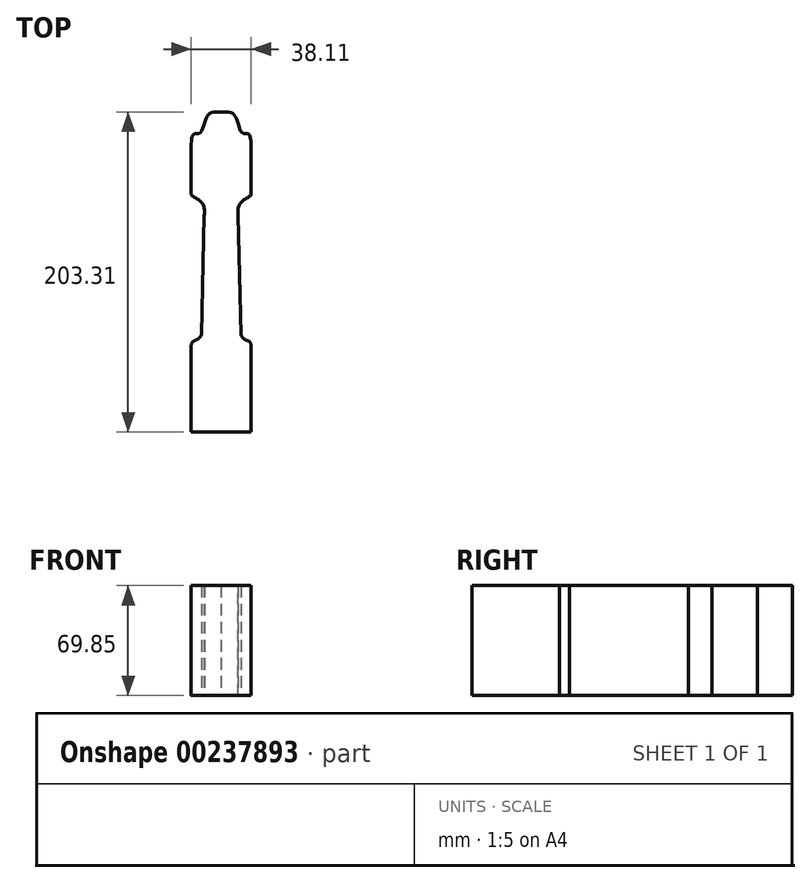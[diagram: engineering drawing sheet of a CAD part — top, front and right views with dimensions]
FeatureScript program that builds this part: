
annotation { "Feature Type Name" : "Feature", "Feature Type Description" : "" }
export const myFeature = defineFeature(function(context is Context, id is Id, definition is map)
    precondition{}
    {
        {
            var Q0;
            Q0=qCreatedBy(makeId("Top.planeOp"),FACE);
            var sketch = newSketch(context, id + "F0", { "sketchPlane" : qUnion([Q0])});
            skLineSegment(sketch, "E0", {"start": v(-63.39, 48.27) * mm, "end": v(-63.39, -154.93) * mm});
            skLineSegment(sketch, "E1", {"start": v(-170.06, 93.3) * mm, "end": v(-170.06, -109.9) * mm});
            skFitSpline(sketch, "E2.MirrorCS", {"points": [v(-170.06, 93.3) * mm, v(-178.63, 91.27) * mm, v(-183.26, 80.39) * mm, v(-187.5, 79.18) * mm, v(-189.1, 71.32) * mm], "startDerivative": vector(-38.08, 2.27) * mm, "endDerivative": vector(-0.76, -41.24) * mm});
            skFitSpline(sketch, "E3", {"points": [v(-189.05, 42.29) * mm, v(-188.9, 40.7) * mm, v(-184.87, 37.86) * mm, v(-181.25, 33.82) * mm, v(-180.84, 27.58) * mm], "startDerivative": vector(-1.25, -12.1) * mm, "endDerivative": vector(-1.29, -22.61) * mm});
            skLineSegment(sketch, "E4", {"start": v(-189.1, -109.9) * mm, "end": v(-189.1, -54.56) * mm});
            skLineSegment(sketch, "E5", {"start": v(-180.84, 27.58) * mm, "end": v(-182.55, -48.01) * mm});
            skFitSpline(sketch, "E6", {"points": [v(-182.55, -48.01) * mm, v(-184.67, -50.84) * mm, v(-188.06, -52.42) * mm, v(-189.1, -54.56) * mm], "startDerivative": vector(-4.75, -9.25) * mm, "endDerivative": vector(-2.08, -8.38) * mm});
            skFitSpline(sketch, "E7.MirrorCS", {"points": [v(-170.06, 93.3) * mm, v(-161.5, 91.27) * mm, v(-156.86, 80.39) * mm, v(-152.62, 79.18) * mm, v(-151, 71.32) * mm], "startDerivative": vector(38.08, 2.27) * mm, "endDerivative": vector(0.76, -41.24) * mm});
            skFitSpline(sketch, "E8.MirrorCS", {"points": [v(-151.07, 42.29) * mm, v(-151.22, 40.7) * mm, v(-155.24, 37.86) * mm, v(-158.87, 33.82) * mm, v(-159.28, 27.58) * mm], "startDerivative": vector(1.25, -12.1) * mm, "endDerivative": vector(1.29, -22.61) * mm});
            skLineSegment(sketch, "E9.MirrorCS", {"start": v(-159.28, 27.58) * mm, "end": v(-157.57, -48.01) * mm});
            skFitSpline(sketch, "E10.MirrorCS", {"points": [v(-157.57, -48.01) * mm, v(-155.45, -50.84) * mm, v(-152.06, -52.42) * mm, v(-151, -54.56) * mm], "startDerivative": vector(4.75, -9.25) * mm, "endDerivative": vector(2.08, -8.38) * mm});
            skLineSegment(sketch, "E11.MirrorCS", {"start": v(-151, -109.9) * mm, "end": v(-151, -54.56) * mm});
            skLineSegment(sketch, "E12", {"start": v(-189.05, 42.29) * mm, "end": v(-189.1, 71.32) * mm});
            skLineSegment(sketch, "E13", {"start": v(-151.07, 42.29) * mm, "end": v(-151, 71.32) * mm});
            skLineSegment(sketch, "E14", {"start": v(-189.1, -109.9) * mm, "end": v(-151, -109.9) * mm});
            skSolve(sketch);
        }
        {
            var Q0;
            {var subQ1=sQuery(id+"F0.wireOp",EDGE,"E1");Q0=makeQuery(id+"F0.imprint","IMPRINT",FACE,{"disambiguationData":[TD([[makeQuery(id+"F0.imprint","IMPRINT",EDGE,{"derivedFrom":subQ1}),-1.0]])]});}
            var Q1;
            {var subQ1=sQuery(id+"F0.wireOp",EDGE,"E1");Q1=makeQuery(id+"F0.imprint","IMPRINT",FACE,{"disambiguationData":[TD([[makeQuery(id+"F0.imprint","IMPRINT",EDGE,{"derivedFrom":subQ1}),1.0]])]});}
            extrude(context, id + "F1", {"entities" : qUnion([Q0, Q1]), "depth" : 69.85 * mm});
        }
        {
            var Q0;
            Q0=makeQuery(id+"F1.opExtrude","SWEPT_BODY",BODY,{"disambiguationData":[OSD([sQuery(id+"F0.wireOp",EDGE,"E2.MirrorCS"),sQuery(id+"F0.wireOp",EDGE,"E3"),sQuery(id+"F0.wireOp",EDGE,"E4"),sQuery(id+"F0.wireOp",EDGE,"E5"),sQuery(id+"F0.wireOp",EDGE,"E6"),sQuery(id+"F0.wireOp",EDGE,"E7.MirrorCS"),sQuery(id+"F0.wireOp",EDGE,"E8.MirrorCS"),sQuery(id+"F0.wireOp",EDGE,"E9.MirrorCS"),sQuery(id+"F0.wireOp",EDGE,"E10.MirrorCS"),sQuery(id+"F0.wireOp",EDGE,"E11.MirrorCS"),sQuery(id+"F0.wireOp",EDGE,"E12"),sQuery(id+"F0.wireOp",EDGE,"E13"),sQuery(id+"F0.wireOp",EDGE,"E14")])]});
            transform(context, id + "F2", {"entities" : qUnion([Q0]), "transformType" : TransformType.TRANSLATION_3D, "dx" : 0 * mm, "dy" : 0 * mm, "dz" : 0 * mm, "makeCopy" : true});
        }
    });
